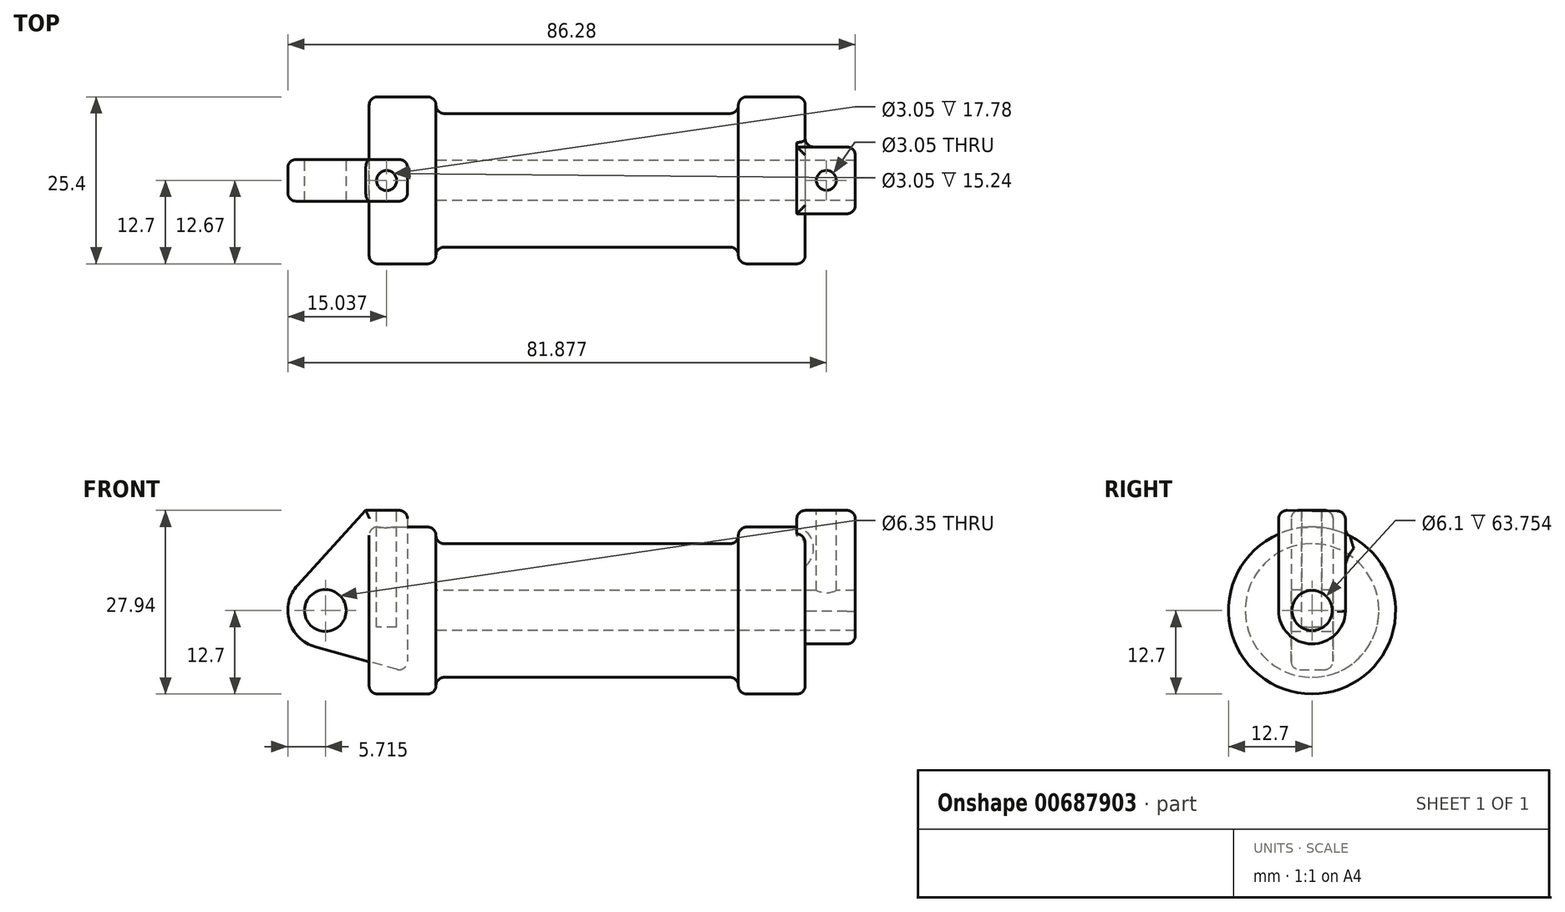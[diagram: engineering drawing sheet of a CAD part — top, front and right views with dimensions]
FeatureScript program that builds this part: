
annotation { "Feature Type Name" : "Feature", "Feature Type Description" : "" }
export const myFeature = defineFeature(function(context is Context, id is Id, definition is map)
    precondition{}
    {
        {
            var Q0;
            Q0=qCreatedBy(makeId("Front.planeOp"),FACE);
            var sketch = newSketch(context, id + "F0", { "sketchPlane" : qUnion([Q0])});
            skLineSegment(sketch, "E0", {"start": v(0, 0) * mm, "end": v(0, 12.7) * mm});
            skLineSegment(sketch, "E1", {"start": v(0, 12.7) * mm, "end": v(10.16, 12.7) * mm});
            skLineSegment(sketch, "E2", {"start": v(10.16, 12.7) * mm, "end": v(10.16, 10.16) * mm});
            skLineSegment(sketch, "E3", {"start": v(10.16, 10.16) * mm, "end": v(56.13, 10.16) * mm});
            skLineSegment(sketch, "E4", {"start": v(56.13, 10.16) * mm, "end": v(56.13, 12.7) * mm});
            skLineSegment(sketch, "E5", {"start": v(56.13, 12.7) * mm, "end": v(66.3, 12.7) * mm});
            skLineSegment(sketch, "E6", {"start": v(66.3, 12.7) * mm, "end": v(66.3, 0) * mm});
            skLineSegment(sketch, "E7", {"start": v(66.3, 0) * mm, "end": v(0, 0) * mm});
            skLineSegment(sketch, "E8", {"start": v(5.84, 15.24) * mm, "end": v(-0.5, 15.24) * mm});
            skLineSegment(sketch, "E9", {"start": v(-0.5, 15.24) * mm, "end": v(-10.88, 3.85) * mm});
            skLineSegment(sketch, "E10", {"start": v(0, 0) * mm, "end": v(-6.65, 0) * mm});
            skCircle(sketch, "E11", {"center": v(-6.65, 0) * mm, "radius": 5.72 * mm});
            skCircle(sketch, "E12", {"center": v(-6.65, 0) * mm, "radius": 3.18 * mm});
            skLineSegment(sketch, "E13", {"start": v(5.84, 15.24) * mm, "end": v(5.84, -9.4) * mm});
            skLineSegment(sketch, "E14", {"start": v(5.84, -9.4) * mm, "end": v(-8.18, -5.5) * mm});
            skSolve(sketch);
        }
        {
            var Q0;
            {var subQ0=sQuery(id+"F0.wireOp",EDGE,"E2");Q0=makeQuery(id+"F0.imprint","IMPRINT",FACE,{"disambiguationData":[TD([[makeQuery(id+"F0.imprint","IMPRINT",EDGE,{"derivedFrom":subQ0}),-1.0]])]});}
            var Q1;
            {var subQ0=sQuery(id+"F0.wireOp",EDGE,"E0");Q1=makeQuery(id+"F0.imprint","IMPRINT",FACE,{"disambiguationData":[TD([[makeQuery(id+"F0.imprint","IMPRINT",EDGE,{"derivedFrom":subQ0}),-1.0]])]});}
            var Q2;
            Q2=sQuery(id+"F0.wireOp",EDGE,"E7");
            revolve(context, id + "F1", {"entities" : qUnion([Q0, Q1]), "axis" : qUnion([Q2]), "revolveType" : RevolveType.FULL});
        }
        {
            var Q0;
            {var subQ5=sQuery(id+"F0.wireOp",EDGE,"E12");Q0=makeQuery(id+"F0.imprint","IMPRINT",FACE,{"disambiguationData":[TD([[makeQuery(id+"F0.imprint","IMPRINT",EDGE,{"derivedFrom":subQ5}),-1.0]])]});}
            var Q1;
            {var subQ1=sQuery(id+"F0.wireOp",EDGE,"E0");Q1=makeQuery(id+"F0.imprint","IMPRINT",FACE,{"disambiguationData":[TD([[makeQuery(id+"F0.imprint","IMPRINT",EDGE,{"derivedFrom":subQ1}),1.0]])]});}
            var Q2;
            {var subQ0=sQuery(id+"F0.wireOp",EDGE,"E14");Q2=makeQuery(id+"F0.imprint","IMPRINT",FACE,{"disambiguationData":[TD([[makeQuery(id+"F0.imprint","IMPRINT",EDGE,{"derivedFrom":subQ0}),-1.0]])]});}
            var Q3;
            {var subQ0=sQuery(id+"F0.wireOp",EDGE,"E0");Q3=makeQuery(id+"F0.imprint","IMPRINT",FACE,{"disambiguationData":[TD([[makeQuery(id+"F0.imprint","IMPRINT",EDGE,{"derivedFrom":subQ0}),-1.0]])]});}
            extrude(context, id + "F2", {"entities" : qUnion([Q0, Q1, Q2, Q3]), "endBound" : BoundingType.SYMMETRIC, "depth" : 6.35 * mm, "offsetDistance" : 25.4 * mm});
        }
        {
            var Q0;
            Q0=makeQuery(id+"F1.opRevolve","SWEPT_FACE",FACE,{"disambiguationData":[OSD([sQuery(id+"F0.wireOp",EDGE,"E6")])]});
            var sketch = newSketch(context, id + "F3", { "sketchPlane" : qUnion([Q0])});
            skCircle(sketch, "E15", {"center": v(0, 0) * mm, "radius": 3.05 * mm});
            skCircle(sketch, "E16", {"center": v(0, 0) * mm, "radius": 5.08 * mm});
            skLineSegment(sketch, "E17", {"start": v(5.08, -0.12) * mm, "end": v(5.08, 15.12) * mm});
            skLineSegment(sketch, "E18", {"start": v(-5.08, 0) * mm, "end": v(-5.08, 15.24) * mm});
            skLineSegment(sketch, "E19", {"start": v(-5.08, 15.24) * mm, "end": v(5.08, 15.12) * mm});
            skSolve(sketch);
        }
        {
            var Q0;
            {var subQ0=sQuery(id+"F3.wireOp",EDGE,"E19");Q0=makeQuery(id+"F3.imprint","IMPRINT",FACE,{"disambiguationData":[TD([[makeQuery(id+"F3.imprint","IMPRINT",EDGE,{"derivedFrom":subQ0}),-1.0]])]});}
            var Q1;
            {var subQ0=sQuery(id+"F3.wireOp",EDGE,"E18");var subQ1=sQuery(id+"F3.wireOp",EDGE,"E16");var subQ2=makeQuery(id+"F3.imprint","INTERSECT",VERTEX,{"derivedFrom":[subQ1,subQ0]});Q1=makeQuery(id+"F3.imprint","IMPRINT",FACE,{"disambiguationData":[TD([[makeQuery(id+"F3.imprint","IMPRINT",EDGE,{"disambiguationData":[TD([[subQ2,1.0]])],"derivedFrom":subQ1}),-1.0]])]});}
            var Q2;
            Q2=makeQuery(id+"F3.imprint","IMPRINT",FACE,{"disambiguationData":[TD([[makeQuery(id+"F3.imprint","IMPRINT",EDGE,{"derivedFrom":sQuery(id+"F3.wireOp",EDGE,"E15")}),-1.0]])]});
            extrude(context, id + "F4", {"entities" : qUnion([Q0, Q1, Q2]), "operationType" : NewBodyOperationType.ADD, "depth" : 7.62 * mm, "offsetDistance" : 25.4 * mm, "hasSecondDirection" : true, "secondDirectionOppositeDirection" : true, "secondDirectionDepth" : 1.27 * mm});
        }
        {
            var Q0;
            Q0=makeQuery(id+"F3.imprint","IMPRINT",FACE,{"disambiguationData":[TD([[makeQuery(id+"F3.imprint","IMPRINT",EDGE,{"derivedFrom":sQuery(id+"F3.wireOp",EDGE,"E15")}),1.0]])]});
            var Q1;
            Q1=makeQuery(id+"F1.opRevolve","SWEPT_FACE",FACE,{"disambiguationData":[OSD([sQuery(id+"F0.wireOp",EDGE,"E2")])]});
            extrude(context, id + "F5", {"entities" : qUnion([Q0]), "operationType" : NewBodyOperationType.REMOVE, "endBound" : BoundingType.UP_TO_SURFACE, "oppositeDirection" : true, "depth" : 25.4 * mm, "endBoundEntityFace" : qUnion([Q1]), "offsetDistance" : 25.4 * mm});
        }
        {
            var Q0;
            Q0=makeQuery(id+"F2.opExtrude","SWEPT_FACE",FACE,{"disambiguationData":[OSD([sQuery(id+"F0.wireOp",EDGE,"E8")])]});
            var sketch = newSketch(context, id + "F6", { "sketchPlane" : qUnion([Q0])});
            skCircle(sketch, "E20", {"center": v(2.67, -0.03) * mm, "radius": 1.52 * mm});
            skPoint(sketch, "E20.centerSnap0", {"position": v(2.67, -3.18) * mm});
            skCircle(sketch, "E21", {"center": v(69.5, 0) * mm, "radius": 1.52 * mm});
            skPoint(sketch, "E21.centerSnap0", {"position": v(5.84, 0) * mm});
            skSolve(sketch);
        }
        {
            var Q0;
            Q0=makeQuery(id+"F6.imprint","IMPRINT",FACE,{"disambiguationData":[TD([[makeQuery(id+"F6.imprint","IMPRINT",EDGE,{"derivedFrom":sQuery(id+"F6.wireOp",EDGE,"E20")}),1.0]])]});
            var Q1;
            Q1=makeQuery(id+"F6.imprint","IMPRINT",FACE,{"disambiguationData":[TD([[makeQuery(id+"F6.imprint","IMPRINT",EDGE,{"derivedFrom":sQuery(id+"F6.wireOp",EDGE,"E21")}),1.0]])]});
            extrude(context, id + "F7", {"entities" : qUnion([Q0, Q1]), "operationType" : NewBodyOperationType.REMOVE, "oppositeDirection" : true, "depth" : 17.78 * mm, "offsetDistance" : 25.4 * mm, "hasSecondDirection" : true, "secondDirectionOppositeDirection" : false, "secondDirectionDepth" : 10.4 * mm});
        }
        {
            var Q0;
            Q0=makeQuery(id+"F1.opRevolve","SWEPT_EDGE",EDGE,{"disambiguationData":[OSD([sQuery(id+"F0.wireOp",EDGE,"E1"),sQuery(id+"F0.wireOp",EDGE,"E2")])]});
            var Q1;
            Q1=makeQuery(id+"F1.opRevolve","SWEPT_FACE",FACE,{"disambiguationData":[OSD([sQuery(id+"F0.wireOp",EDGE,"E2")])]});
            var Q2;
            Q2=makeQuery(id+"F2.opExtrude","CAP_EDGE",EDGE,{"disambiguationData":[OSD([sQuery(id+"F0.wireOp",EDGE,"E8")])],"isStart":false});
            var Q3;
            Q3=makeQuery(id+"F2.opExtrude","CAP_EDGE",EDGE,{"disambiguationData":[OSD([sQuery(id+"F0.wireOp",EDGE,"E9")])],"isStart":false});
            var Q4;
            Q4=makeQuery(id+"F2.opExtrude","CAP_EDGE",EDGE,{"disambiguationData":[OSD([sQuery(id+"F0.wireOp",EDGE,"E9")])],"isStart":true});
            var Q5;
            Q5=makeQuery(id+"F2.opExtrude","CAP_EDGE",EDGE,{"disambiguationData":[OSD([sQuery(id+"F0.wireOp",EDGE,"E8")])],"isStart":true});
            var Q6;
            Q6=makeQuery(id+"F2.opExtrude","SWEPT_EDGE",EDGE,{"disambiguationData":[OSD([sQuery(id+"F0.wireOp",EDGE,"E8"),sQuery(id+"F0.wireOp",EDGE,"E13")])]});
            var Q7;
            Q7=makeQuery(id+"F2.opExtrude","SWEPT_FACE",FACE,{"disambiguationData":[OSD([sQuery(id+"F0.wireOp",EDGE,"E13")])]});
            var Q8;
            Q8=makeQuery(id+"F1.opRevolve","SWEPT_EDGE",EDGE,{"disambiguationData":[OSD([sQuery(id+"F0.wireOp",EDGE,"E3"),sQuery(id+"F0.wireOp",EDGE,"E4")])]});
            var Q9;
            Q9=makeQuery(id+"F1.opRevolve","SWEPT_EDGE",EDGE,{"disambiguationData":[OSD([sQuery(id+"F0.wireOp",EDGE,"E4"),sQuery(id+"F0.wireOp",EDGE,"E5")])]});
            var Q10;
            Q10=makeQuery(id+"F1.opRevolve","SWEPT_EDGE",EDGE,{"disambiguationData":[OSD([sQuery(id+"F0.wireOp",EDGE,"E5"),sQuery(id+"F0.wireOp",EDGE,"E6")])]});
            var Q11;
            Q11=makeQuery(id+"F4.opExtrude","CAP_EDGE",EDGE,{"disambiguationData":[OSD([sQuery(id+"F3.wireOp",EDGE,"E17")])],"isStart":false});
            var Q12;
            Q12=makeQuery(id+"F4.opExtrude","CAP_EDGE",EDGE,{"disambiguationData":[OSD([sQuery(id+"F3.wireOp",EDGE,"E18")])],"isStart":false});
            var Q13;
            Q13=makeQuery(id+"F4.opExtrude","CAP_EDGE",EDGE,{"disambiguationData":[OSD([sQuery(id+"F3.wireOp",EDGE,"E16")])],"isStart":false});
            var Q14;
            Q14=makeQuery(id+"F4.opExtrude","CAP_EDGE",EDGE,{"disambiguationData":[OSD([sQuery(id+"F3.wireOp",EDGE,"E19")])],"isStart":false});
            var Q15;
            Q15=makeQuery(id+"F4.boolean.opBoolean","INTERSECT",EDGE,{"derivedFrom":[makeQuery(id+"F1.opRevolve","SWEPT_FACE",FACE,{"disambiguationData":[OSD([sQuery(id+"F0.wireOp",EDGE,"E5")])]}),makeQuery(id+"F4.opExtrude","SWEPT_FACE",FACE,{"disambiguationData":[OSD([sQuery(id+"F3.wireOp",EDGE,"E17")])]})]});
            var Q16;
            Q16=makeQuery(id+"F4.opExtrude","SWEPT_EDGE",EDGE,{"disambiguationData":[OSD([sQuery(id+"F3.wireOp",EDGE,"E18"),sQuery(id+"F3.wireOp",EDGE,"E19")])]});
            var Q17;
            Q17=makeQuery(id+"F4.opExtrude","CAP_EDGE",EDGE,{"disambiguationData":[OSD([sQuery(id+"F3.wireOp",EDGE,"E19")])],"isStart":true});
            var Q18;
            Q18=makeQuery(id+"F4.opExtrude","SWEPT_EDGE",EDGE,{"disambiguationData":[OSD([sQuery(id+"F3.wireOp",EDGE,"E17"),sQuery(id+"F3.wireOp",EDGE,"E19")])]});
            var Q19;
            Q19=makeQuery(id+"F1.opRevolve","SWEPT_EDGE",EDGE,{"disambiguationData":[OSD([sQuery(id+"F0.wireOp",EDGE,"E0"),sQuery(id+"F0.wireOp",EDGE,"E1")])]});
            fillet(context, id + "F8", {"entities" : qUnion([Q0, Q1, Q2, Q3, Q4, Q5, Q6, Q7, Q8, Q9, Q10, Q11, Q12, Q13, Q14, Q15, Q16, Q17, Q18, Q19]), "radius" : 1.27 * mm, "tangentPropagation" : true, "allowEdgeOverflow" : false});
        }
    });
